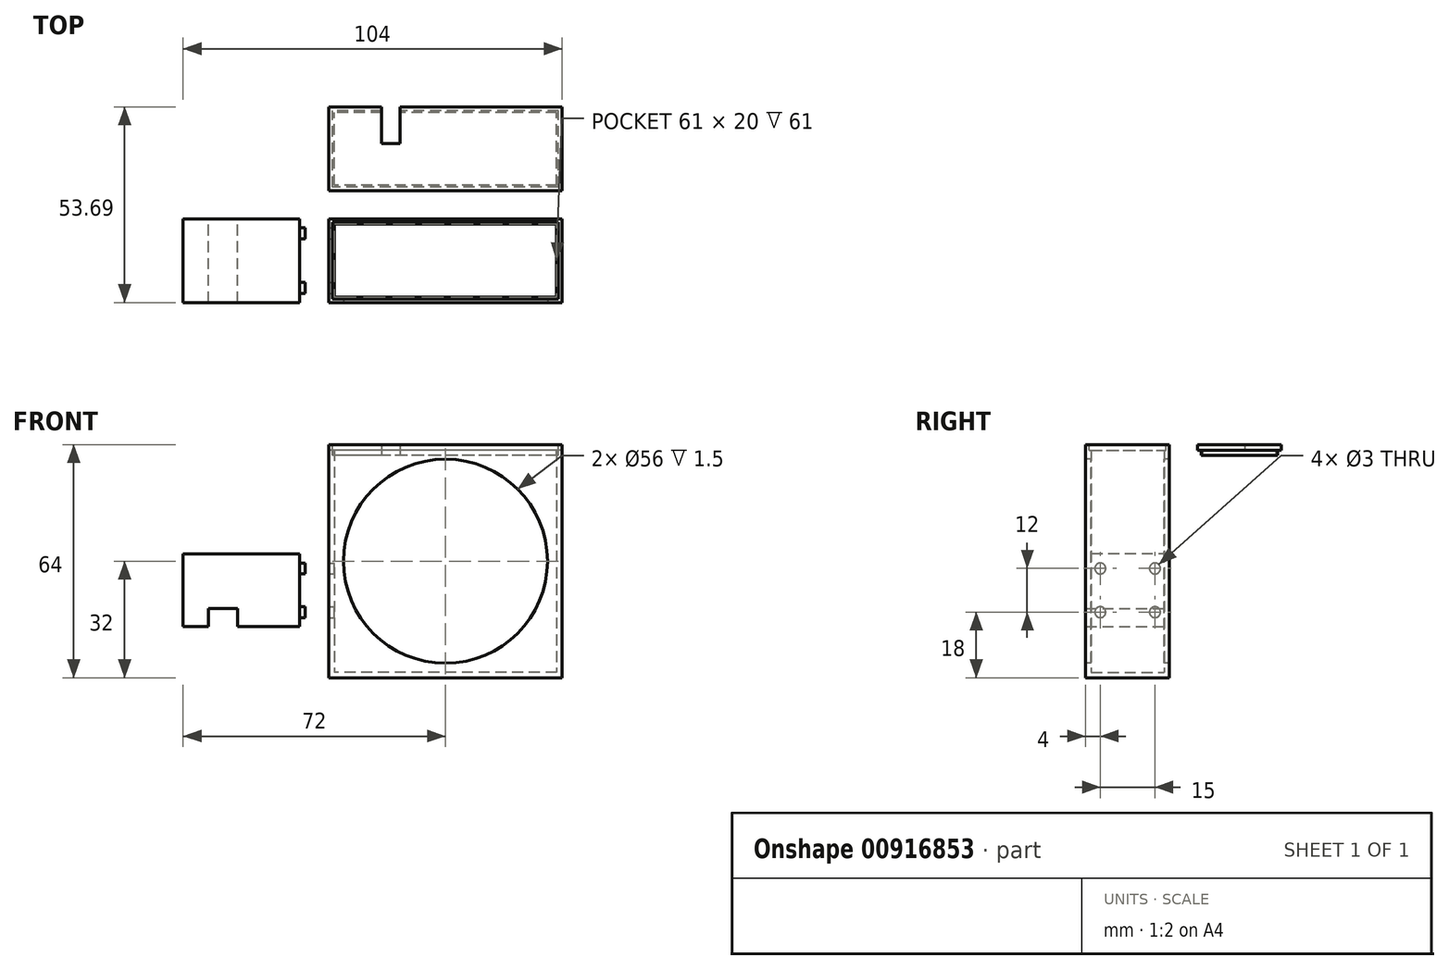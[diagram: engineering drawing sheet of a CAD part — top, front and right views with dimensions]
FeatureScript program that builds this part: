
annotation { "Feature Type Name" : "Feature", "Feature Type Description" : "" }
export const myFeature = defineFeature(function(context is Context, id is Id, definition is map)
    precondition{}
    {
        {
            var Q0;
            Q0=qCreatedBy(makeId("Front.planeOp"),FACE);
            var sketch = newSketch(context, id + "F0", { "sketchPlane" : qUnion([Q0])});
            skLineSegment(sketch, "E0.bottom", {"start": v(32, 32) * mm, "end": v(-32, 32) * mm});
            skLineSegment(sketch, "E0.top", {"start": v(32, -32) * mm, "end": v(-32, -32) * mm});
            skLineSegment(sketch, "E0.left", {"start": v(32, 32) * mm, "end": v(32, -32) * mm});
            skLineSegment(sketch, "E0.right", {"start": v(-32, 32) * mm, "end": v(-32, -32) * mm});
            skPoint(sketch, "E0.middle", {"position": v(0, 0) * mm});
            skCircle(sketch, "E1", {"center": v(0, 0) * mm, "radius": 28 * mm});
            skSolve(sketch);
        }
        {
            var Q0;
            Q0=makeQuery(id+"F0.imprint","IMPRINT",FACE,{"disambiguationData":[TD([[makeQuery(id+"F0.imprint","IMPRINT",EDGE,{"derivedFrom":sQuery(id+"F0.wireOp",EDGE,"E0.bottom")}),1.0]])]});
            extrude(context, id + "F1", {"entities" : qUnion([Q0]), "oppositeDirection" : true, "depth" : 1.5 * mm, "offsetDistance" : 25 * mm});
        }
        {
            var Q0;
            Q0=makeQuery(id+"F1.opExtrude","SWEPT_FACE",FACE,{"disambiguationData":[OSD([sQuery(id+"F0.wireOp",EDGE,"E0.top")])]});
            var sketch = newSketch(context, id + "F2", { "sketchPlane" : qUnion([Q0])});
            skLineSegment(sketch, "E2.bottom", {"start": v(-32, 21.5) * mm, "end": v(32, 21.5) * mm});
            skLineSegment(sketch, "E2.top", {"start": v(-32, -1.5) * mm, "end": v(32, -1.5) * mm});
            skLineSegment(sketch, "E2.left", {"start": v(-32, 21.5) * mm, "end": v(-32, -1.5) * mm});
            skLineSegment(sketch, "E2.right", {"start": v(32, 21.5) * mm, "end": v(32, -1.5) * mm});
            skPoint(sketch, "E2.middle", {"position": v(0, 10) * mm});
            skSolve(sketch);
        }
        {
            var Q0;
            {var subQ0=sQuery(id+"F2.wireOp",EDGE,"E2.bottom");Q0=makeQuery(id+"F2.imprint","IMPRINT",FACE,{"disambiguationData":[TD([[makeQuery(id+"F2.imprint","IMPRINT",EDGE,{"derivedFrom":subQ0}),-1.0]])]});}
            extrude(context, id + "F3", {"entities" : qUnion([Q0]), "operationType" : NewBodyOperationType.ADD, "oppositeDirection" : true, "depth" : 1.5 * mm, "offsetDistance" : 25 * mm});
        }
        {
            var Q0;
            {var subQ0=sQuery(id+"F0.wireOp",EDGE,"E0.top");Q0=makeQuery(id+"F3.boolean.opBoolean","MERGE",FACE,{"derivedFrom":[makeQuery(id+"F1.opExtrude","SWEPT_FACE",FACE,{"disambiguationData":[OSD([subQ0])]}),makeQuery(id+"F3.opExtrude","CAP_FACE",FACE,{"disambiguationData":[OSD([subQ0,sQuery(id+"F2.wireOp",EDGE,"E2.bottom"),sQuery(id+"F2.wireOp",EDGE,"E2.left"),sQuery(id+"F2.wireOp",EDGE,"E2.right")])],"isStart":true})]});}
            var sketch = newSketch(context, id + "F4", { "sketchPlane" : qUnion([Q0])});
            skLineSegment(sketch, "E3.bottom", {"start": v(-32, 21.5) * mm, "end": v(-30.5, 21.5) * mm});
            skLineSegment(sketch, "E3.top", {"start": v(-32, -1.5) * mm, "end": v(-30.5, -1.5) * mm});
            skLineSegment(sketch, "E3.left", {"start": v(-32, 21.5) * mm, "end": v(-32, -1.5) * mm});
            skLineSegment(sketch, "E3.right", {"start": v(-30.5, 21.5) * mm, "end": v(-30.5, -1.5) * mm});
            skLineSegment(sketch, "E4.bottom", {"start": v(30.5, 21.5) * mm, "end": v(32, 21.5) * mm});
            skLineSegment(sketch, "E4.top", {"start": v(30.5, -1.5) * mm, "end": v(32, -1.5) * mm});
            skLineSegment(sketch, "E4.left", {"start": v(30.5, 21.5) * mm, "end": v(30.5, -1.5) * mm});
            skLineSegment(sketch, "E4.right", {"start": v(32, 21.5) * mm, "end": v(32, -1.5) * mm});
            skSolve(sketch);
        }
        {
            var Q0;
            Q0 = qSketchRegion(id + "F4", true);
            extrude(context, id + "F5", {"entities" : qUnion([Q0]), "operationType" : NewBodyOperationType.ADD, "oppositeDirection" : true, "depth" : 64 * mm, "offsetDistance" : 25 * mm});
        }
        {
            var Q0;
            Q0=makeQuery(id+"F5.boolean.opBoolean","MERGE",FACE,{"derivedFrom":[makeQuery(id+"F3.opExtrude","SWEPT_FACE",FACE,{"disambiguationData":[OSD([sQuery(id+"F2.wireOp",EDGE,"E2.bottom")])]}),makeQuery(id+"F5.opExtrude","SWEPT_FACE",FACE,{"disambiguationData":[OSD([sQuery(id+"F4.wireOp",EDGE,"E3.bottom")])]}),makeQuery(id+"F5.opExtrude","SWEPT_FACE",FACE,{"disambiguationData":[OSD([sQuery(id+"F4.wireOp",EDGE,"E4.bottom")])]})]});
            var sketch = newSketch(context, id + "F6", { "sketchPlane" : qUnion([Q0])});
            skLineSegment(sketch, "E5.bottom", {"start": v(-32, 32) * mm, "end": v(32, 32) * mm});
            skLineSegment(sketch, "E5.top", {"start": v(-32, -32) * mm, "end": v(32, -32) * mm});
            skLineSegment(sketch, "E5.left", {"start": v(-32, 32) * mm, "end": v(-32, -32) * mm});
            skLineSegment(sketch, "E5.right", {"start": v(32, 32) * mm, "end": v(32, -32) * mm});
            skPoint(sketch, "E5.middle", {"position": v(0, 0) * mm});
            skCircle(sketch, "E6", {"center": v(0, 0) * mm, "radius": 28 * mm});
            skSolve(sketch);
        }
        {
            var Q0;
            Q0=makeQuery(id+"F6.imprint","IMPRINT",FACE,{"disambiguationData":[TD([[makeQuery(id+"F6.imprint","IMPRINT",EDGE,{"derivedFrom":sQuery(id+"F6.wireOp",EDGE,"E6")}),-1.0]])]});
            extrude(context, id + "F7", {"entities" : qUnion([Q0]), "operationType" : NewBodyOperationType.ADD, "oppositeDirection" : true, "depth" : 1.5 * mm, "offsetDistance" : 25 * mm});
        }
        {
            var Q0;
            Q0=makeQuery(id+"F7.boolean.opBoolean","MERGE",FACE,{"derivedFrom":[makeQuery(id+"F5.boolean.opBoolean","MERGE",FACE,{"derivedFrom":[makeQuery(id+"F1.opExtrude","SWEPT_FACE",FACE,{"disambiguationData":[OSD([sQuery(id+"F0.wireOp",EDGE,"E0.bottom")])]}),makeQuery(id+"F5.opExtrude","CAP_FACE",FACE,{"disambiguationData":[OSD([sQuery(id+"F4.wireOp",EDGE,"E3.bottom"),sQuery(id+"F4.wireOp",EDGE,"E3.top"),sQuery(id+"F4.wireOp",EDGE,"E3.left"),sQuery(id+"F4.wireOp",EDGE,"E3.right")])],"isStart":false}),makeQuery(id+"F5.opExtrude","CAP_FACE",FACE,{"disambiguationData":[OSD([sQuery(id+"F4.wireOp",EDGE,"E4.bottom"),sQuery(id+"F4.wireOp",EDGE,"E4.top"),sQuery(id+"F4.wireOp",EDGE,"E4.left"),sQuery(id+"F4.wireOp",EDGE,"E4.right")])],"isStart":false})]}),makeQuery(id+"F7.opExtrude","SWEPT_FACE",FACE,{"disambiguationData":[OSD([sQuery(id+"F6.wireOp",EDGE,"E5.bottom")])]})]});
            var sketch = newSketch(context, id + "F8", { "sketchPlane" : qUnion([Q0])});
            skLineSegment(sketch, "E7.bottom", {"start": v(32, 32.2) * mm, "end": v(-32, 32.2) * mm});
            skLineSegment(sketch, "E7.top", {"start": v(32, 9.2) * mm, "end": v(-32, 9.2) * mm});
            skLineSegment(sketch, "E7.left", {"start": v(32, 32.2) * mm, "end": v(32, 9.2) * mm});
            skLineSegment(sketch, "E7.right", {"start": v(-32, 32.2) * mm, "end": v(-32, 9.2) * mm});
            skPoint(sketch, "E7.middle", {"position": v(0, 20.7) * mm});
            skSolve(sketch);
        }
        {
            var Q0;
            Q0 = qSketchRegion(id + "F8", true);
            extrude(context, id + "F9", {"entities" : qUnion([Q0]), "oppositeDirection" : true, "depth" : 1.5 * mm, "offsetDistance" : 25 * mm});
        }
        {
            var Q0;
            Q0=makeQuery(id+"F9.opExtrude","CAP_FACE",FACE,{"disambiguationData":[OSD([sQuery(id+"F8.wireOp",EDGE,"E7.bottom"),sQuery(id+"F8.wireOp",EDGE,"E7.top"),sQuery(id+"F8.wireOp",EDGE,"E7.left"),sQuery(id+"F8.wireOp",EDGE,"E7.right")])],"isStart":false});
            var sketch = newSketch(context, id + "F10", { "sketchPlane" : qUnion([Q0])});
            skLineSegment(sketch, "E8.bottom", {"start": v(31, -10.2) * mm, "end": v(-31, -10.2) * mm});
            skLineSegment(sketch, "E8.top", {"start": v(31, -31.2) * mm, "end": v(-31, -31.2) * mm});
            skLineSegment(sketch, "E8.left", {"start": v(31, -10.2) * mm, "end": v(31, -31.2) * mm});
            skLineSegment(sketch, "E8.right", {"start": v(-31, -10.2) * mm, "end": v(-31, -31.2) * mm});
            skLineSegment(sketch, "E9.bottom", {"start": v(30.5, -10.7) * mm, "end": v(-30.5, -10.7) * mm});
            skLineSegment(sketch, "E9.top", {"start": v(30.5, -30.7) * mm, "end": v(-30.5, -30.7) * mm});
            skLineSegment(sketch, "E9.left", {"start": v(30.5, -10.7) * mm, "end": v(30.5, -30.7) * mm});
            skLineSegment(sketch, "E9.right", {"start": v(-30.5, -10.7) * mm, "end": v(-30.5, -30.7) * mm});
            skSolve(sketch);
        }
        {
            var Q0;
            Q0=makeQuery(id+"F10.imprint","IMPRINT",FACE,{"disambiguationData":[TD([[makeQuery(id+"F10.imprint","IMPRINT",EDGE,{"derivedFrom":sQuery(id+"F10.wireOp",EDGE,"E8.bottom")}),1.0]])]});
            extrude(context, id + "F11", {"entities" : qUnion([Q0]), "operationType" : NewBodyOperationType.ADD, "depth" : 1.5 * mm, "offsetDistance" : 25 * mm});
        }
        {
            var Q0;
            Q0=makeQuery(id+"F7.boolean.opBoolean","MERGE",FACE,{"derivedFrom":[makeQuery(id+"F5.boolean.opBoolean","MERGE",FACE,{"derivedFrom":[makeQuery(id+"F1.opExtrude","SWEPT_FACE",FACE,{"disambiguationData":[OSD([sQuery(id+"F0.wireOp",EDGE,"E0.bottom")])]}),makeQuery(id+"F5.opExtrude","CAP_FACE",FACE,{"disambiguationData":[OSD([sQuery(id+"F4.wireOp",EDGE,"E3.bottom"),sQuery(id+"F4.wireOp",EDGE,"E3.top"),sQuery(id+"F4.wireOp",EDGE,"E3.left"),sQuery(id+"F4.wireOp",EDGE,"E3.right")])],"isStart":false}),makeQuery(id+"F5.opExtrude","CAP_FACE",FACE,{"disambiguationData":[OSD([sQuery(id+"F4.wireOp",EDGE,"E4.bottom"),sQuery(id+"F4.wireOp",EDGE,"E4.top"),sQuery(id+"F4.wireOp",EDGE,"E4.left"),sQuery(id+"F4.wireOp",EDGE,"E4.right")])],"isStart":false})]}),makeQuery(id+"F7.opExtrude","SWEPT_FACE",FACE,{"disambiguationData":[OSD([sQuery(id+"F6.wireOp",EDGE,"E5.bottom")])]})]});
            var sketch = newSketch(context, id + "F12", { "sketchPlane" : qUnion([Q0])});
            skLineSegment(sketch, "E10.bottom", {"start": v(31, -20.5) * mm, "end": v(-31, -20.5) * mm});
            skLineSegment(sketch, "E10.top", {"start": v(31, 0.5) * mm, "end": v(-31, 0.5) * mm});
            skLineSegment(sketch, "E10.left", {"start": v(31, -20.5) * mm, "end": v(31, 0.5) * mm});
            skLineSegment(sketch, "E10.right", {"start": v(-31, -20.5) * mm, "end": v(-31, 0.5) * mm});
            skSolve(sketch);
        }
        {
            var Q0;
            Q0=makeQuery(id+"F12.imprint","IMPRINT",FACE,{"disambiguationData":[TD([[makeQuery(id+"F12.imprint","IMPRINT",EDGE,{"derivedFrom":sQuery(id+"F12.wireOp",EDGE,"E10.bottom")}),-1.0]])]});
            extrude(context, id + "F13", {"entities" : qUnion([Q0]), "operationType" : NewBodyOperationType.REMOVE, "oppositeDirection" : true, "depth" : 1.5 * mm, "offsetDistance" : 25 * mm});
        }
        {
            var Q0;
            Q0=makeQuery(id+"F9.opExtrude","SWEPT_FACE",FACE,{"disambiguationData":[OSD([sQuery(id+"F8.wireOp",EDGE,"E7.bottom")])]});
            var sketch = newSketch(context, id + "F14", { "sketchPlane" : qUnion([Q0])});
            skLineSegment(sketch, "E11.bottom", {"start": v(12.5, 32) * mm, "end": v(17.5, 32) * mm});
            skLineSegment(sketch, "E11.top", {"start": v(12.5, 29) * mm, "end": v(17.5, 29) * mm});
            skLineSegment(sketch, "E11.left", {"start": v(12.5, 32) * mm, "end": v(12.5, 30.5) * mm});
            skLineSegment(sketch, "E11.right", {"start": v(17.5, 32) * mm, "end": v(17.5, 30.5) * mm});
            skLineSegment(sketch, "E12", {"start": v(12.5, 30.5) * mm, "end": v(12.5, 29) * mm});
            skLineSegment(sketch, "E13", {"start": v(17.5, 30.5) * mm, "end": v(17.5, 29) * mm});
            skSolve(sketch);
        }
        {
            var Q0;
            Q0=makeQuery(id+"F14.imprint","IMPRINT",FACE,{"disambiguationData":[TD([[makeQuery(id+"F14.imprint","IMPRINT",EDGE,{"derivedFrom":sQuery(id+"F14.wireOp",EDGE,"E11.bottom")}),-1.0]])]});
            var Q1;
            {var subQ0=sQuery(id+"F14.wireOp",EDGE,"E11.top");Q1=makeQuery(id+"F14.imprint","IMPRINT",FACE,{"disambiguationData":[TD([[makeQuery(id+"F14.imprint","IMPRINT",EDGE,{"derivedFrom":subQ0}),1.0]])]});}
            extrude(context, id + "F15", {"entities" : qUnion([Q0, Q1]), "operationType" : NewBodyOperationType.REMOVE, "oppositeDirection" : true, "depth" : 10 * mm, "offsetDistance" : 25 * mm});
        }
        {
            var Q0;
            Q0=makeQuery(id+"F5.boolean.opBoolean","MERGE",FACE,{"derivedFrom":[makeQuery(id+"F3.boolean.opBoolean","MERGE",FACE,{"derivedFrom":[makeQuery(id+"F1.opExtrude","SWEPT_FACE",FACE,{"disambiguationData":[OSD([sQuery(id+"F0.wireOp",EDGE,"E0.right")])]}),makeQuery(id+"F3.opExtrude","SWEPT_FACE",FACE,{"disambiguationData":[OSD([sQuery(id+"F2.wireOp",EDGE,"E2.left")])]})]}),makeQuery(id+"F5.opExtrude","SWEPT_FACE",FACE,{"disambiguationData":[OSD([sQuery(id+"F4.wireOp",EDGE,"E3.left")])]})]});
            cPlane(context, id + "F16", {"entities" : qUnion([Q0]), "cplaneType" : CPlaneType.OFFSET, "offset" : 8 * mm, "width" : 150 * mm, "height" : 150 * mm});
        }
        {
            var Q0;
            Q0=qCreatedBy(id+"F16.planeOp",FACE);
            var sketch = newSketch(context, id + "F17", { "sketchPlane" : qUnion([Q0])});
            skLineSegment(sketch, "E14.bottom", {"start": v(-1.5, -18) * mm, "end": v(21.5, -18) * mm});
            skLineSegment(sketch, "E14.top", {"start": v(-1.5, 2) * mm, "end": v(21.5, 2) * mm});
            skLineSegment(sketch, "E14.left", {"start": v(-1.5, -18) * mm, "end": v(-1.5, 2) * mm});
            skLineSegment(sketch, "E14.right", {"start": v(21.5, -18) * mm, "end": v(21.5, 2) * mm});
            skSolve(sketch);
        }
        {
            var Q0;
            Q0=makeQuery(id+"F17.imprint","IMPRINT",FACE,{"disambiguationData":[TD([[makeQuery(id+"F17.imprint","IMPRINT",EDGE,{"derivedFrom":sQuery(id+"F17.wireOp",EDGE,"E14.bottom")}),1.0]])]});
            extrude(context, id + "F18", {"entities" : qUnion([Q0]), "depth" : 32 * mm, "offsetDistance" : 25 * mm});
        }
        {
            var Q0;
            Q0=makeQuery(id+"F18.opExtrude","SWEPT_FACE",FACE,{"disambiguationData":[OSD([sQuery(id+"F17.wireOp",EDGE,"E14.bottom")])]});
            var sketch = newSketch(context, id + "F19", { "sketchPlane" : qUnion([Q0])});
            skLineSegment(sketch, "E15.bottom", {"start": v(-65, 21.5) * mm, "end": v(-57, 21.5) * mm});
            skLineSegment(sketch, "E15.top", {"start": v(-65, -1.5) * mm, "end": v(-57, -1.5) * mm});
            skLineSegment(sketch, "E15.left", {"start": v(-65, 21.5) * mm, "end": v(-65, -1.5) * mm});
            skLineSegment(sketch, "E15.right", {"start": v(-57, 21.5) * mm, "end": v(-57, -1.5) * mm});
            skSolve(sketch);
        }
        {
            var Q0;
            Q0=makeQuery(id+"F19.imprint","IMPRINT",FACE,{"disambiguationData":[TD([[makeQuery(id+"F19.imprint","IMPRINT",EDGE,{"derivedFrom":sQuery(id+"F19.wireOp",EDGE,"E15.bottom")}),-1.0]])]});
            extrude(context, id + "F20", {"entities" : qUnion([Q0]), "operationType" : NewBodyOperationType.REMOVE, "oppositeDirection" : true, "depth" : 5 * mm, "offsetDistance" : 25 * mm});
        }
        {
            var Q0;
            Q0=makeQuery(id+"F18.opExtrude","CAP_FACE",FACE,{"disambiguationData":[OSD([sQuery(id+"F17.wireOp",EDGE,"E14.bottom"),sQuery(id+"F17.wireOp",EDGE,"E14.top"),sQuery(id+"F17.wireOp",EDGE,"E14.left"),sQuery(id+"F17.wireOp",EDGE,"E14.right")])],"isStart":true});
            var sketch = newSketch(context, id + "F21", { "sketchPlane" : qUnion([Q0])});
            skCircle(sketch, "E16", {"center": v(-17.5, -2) * mm, "radius": 1.5 * mm});
            skCircle(sketch, "E17", {"center": v(-17.5, -14) * mm, "radius": 1.5 * mm});
            skCircle(sketch, "E18", {"center": v(-2.5, -2) * mm, "radius": 1.5 * mm});
            skCircle(sketch, "E19", {"center": v(-2.5, -14) * mm, "radius": 1.5 * mm});
            skSolve(sketch);
        }
        {
            var Q0;
            Q0 = qSketchRegion(id + "F21", true);
            extrude(context, id + "F22", {"entities" : qUnion([Q0]), "operationType" : NewBodyOperationType.ADD, "depth" : 1.5 * mm, "offsetDistance" : 25 * mm});
        }
        {
            var Q0;
            Q0=makeQuery(id+"F5.opExtrude","SWEPT_FACE",FACE,{"disambiguationData":[OSD([sQuery(id+"F4.wireOp",EDGE,"E3.right")])]});
            var sketch = newSketch(context, id + "F23", { "sketchPlane" : qUnion([Q0])});
            skCircle(sketch, "E20", {"center": v(-2.5, -2) * mm, "radius": 1.5 * mm});
            skCircle(sketch, "E21", {"center": v(-2.5, -14) * mm, "radius": 1.5 * mm});
            skCircle(sketch, "E22", {"center": v(-17.5, -14) * mm, "radius": 1.5 * mm});
            skCircle(sketch, "E23", {"center": v(-17.5, -2) * mm, "radius": 1.5 * mm});
            skSolve(sketch);
        }
        {
            var Q0;
            Q0 = qSketchRegion(id + "F23", true);
            extrude(context, id + "F24", {"entities" : qUnion([Q0]), "operationType" : NewBodyOperationType.REMOVE, "oppositeDirection" : true, "depth" : 4 * mm, "offsetDistance" : 25 * mm});
        }
    });
